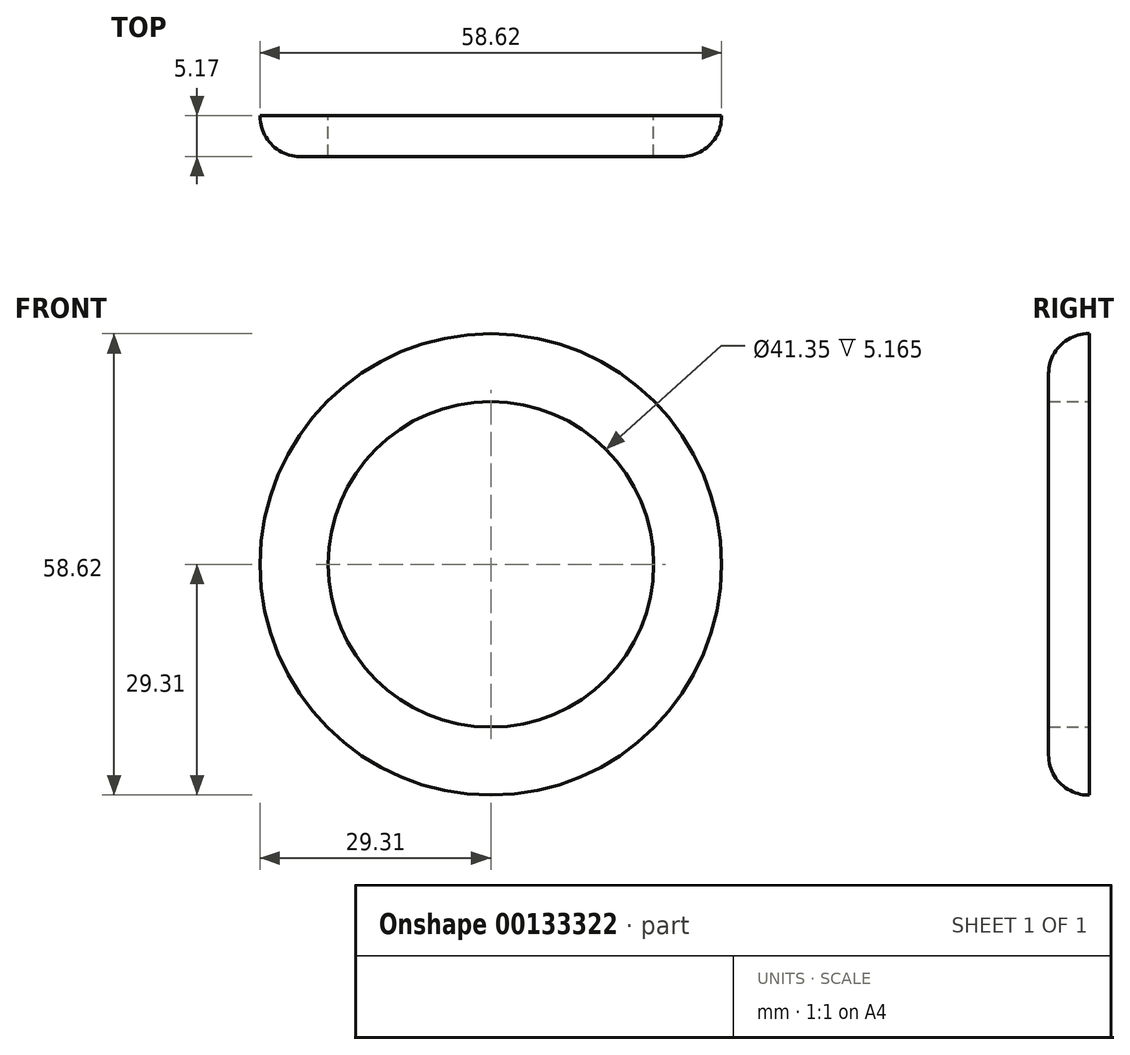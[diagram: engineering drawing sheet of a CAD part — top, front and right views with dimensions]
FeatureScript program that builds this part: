
annotation { "Feature Type Name" : "Feature", "Feature Type Description" : "" }
export const myFeature = defineFeature(function(context is Context, id is Id, definition is map)
    precondition{}
    {
        {
            var Q0;
            Q0=qCreatedBy(makeId("Front.planeOp"),FACE);
            var sketch = newSketch(context, id + "F0", { "sketchPlane" : qUnion([Q0])});
            skCircle(sketch, "E0", {"center": v(0, 0) * mm, "radius": 29.31 * mm});
            skCircle(sketch, "E1.0", {"center": v(0, 0) * mm, "radius": 13.92 * mm});
            skCircle(sketch, "E2.0", {"center": v(0, 0) * mm, "radius": 20.68 * mm});
            skSolve(sketch);
        }
        {
            var Q0;
            Q0 = qSketchRegion(id + "F0", true);
            extrude(context, id + "F1", {"entities" : qUnion([Q0]), "depth" : 5.17 * mm});
        }
        {
            var Q0;
            Q0=makeQuery(id+"F1.opExtrude","CAP_EDGE",EDGE,{"disambiguationData":[OSD([sQuery(id+"F0.wireOp",EDGE,"E0")])],"isStart":false});
            fillet(context, id + "F2", {"entities" : qUnion([Q0]), "radius" : 5.08 * mm, "tangentPropagation" : true, "allowEdgeOverflow" : false});
        }
    });
